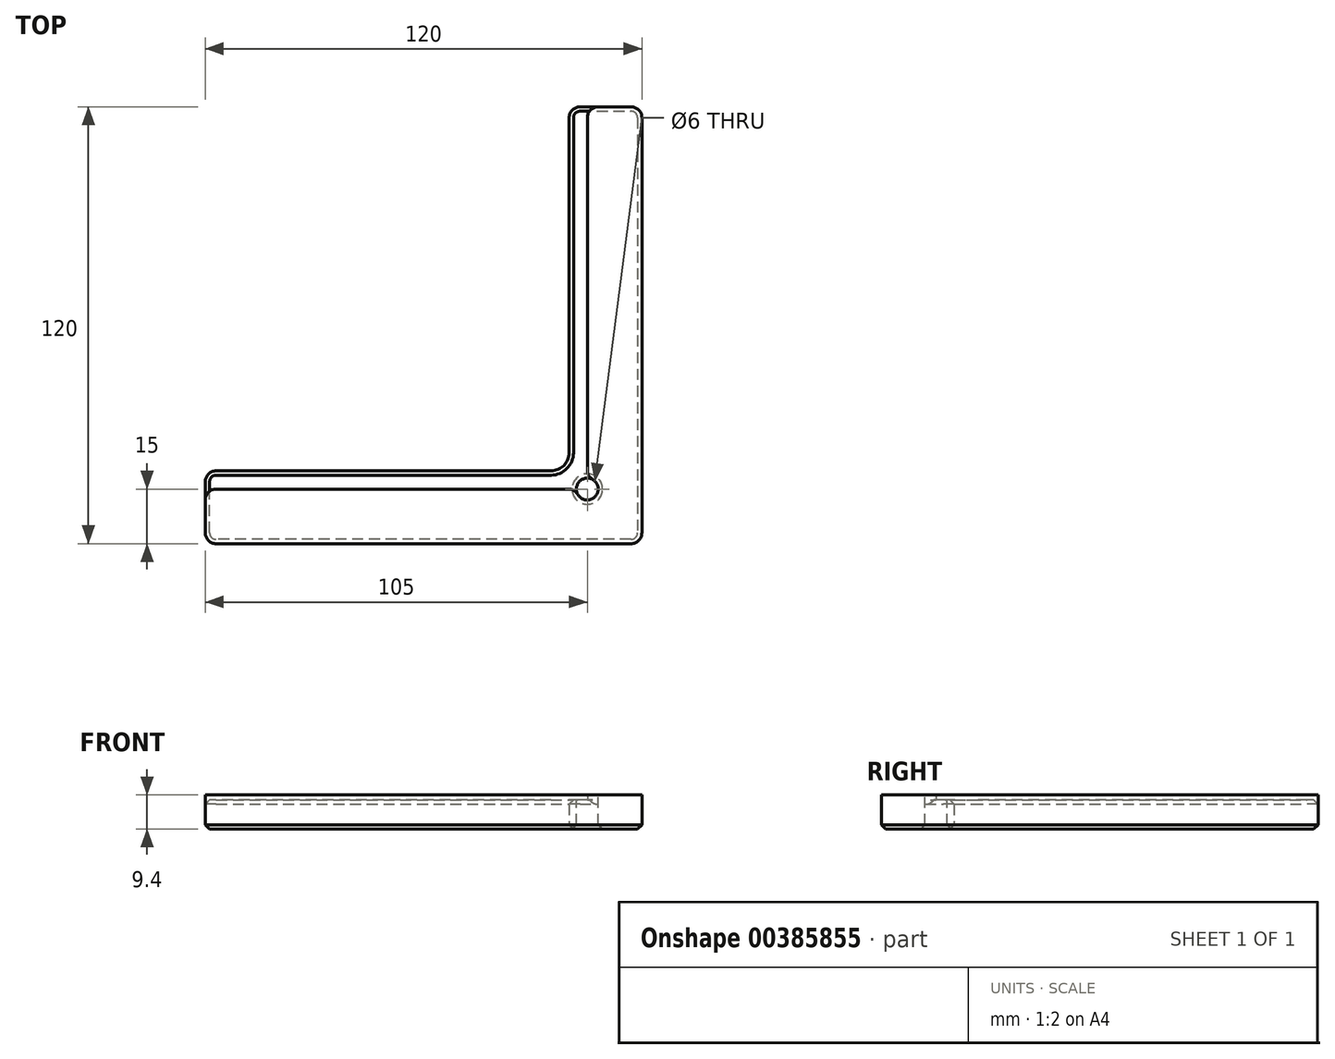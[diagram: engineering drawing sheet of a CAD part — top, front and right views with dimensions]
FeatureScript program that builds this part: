
annotation { "Feature Type Name" : "Feature", "Feature Type Description" : "" }
export const myFeature = defineFeature(function(context is Context, id is Id, definition is map)
    precondition{}
    {
        {
            var Q0;
            Q0=qCreatedBy(makeId("Top.planeOp"),FACE);
            var sketch = newSketch(context, id + "F0", { "sketchPlane" : qUnion([Q0])});
            skLineSegment(sketch, "E0", {"start": v(0, 120) * mm, "end": v(0, 0) * mm});
            skLineSegment(sketch, "E1", {"start": v(0, 0) * mm, "end": v(-120, 0) * mm});
            skLineSegment(sketch, "E2", {"start": v(-120, 0) * mm, "end": v(-120, 20) * mm});
            skLineSegment(sketch, "E3", {"start": v(-120, 20) * mm, "end": v(-20, 20) * mm});
            skLineSegment(sketch, "E4", {"start": v(-20, 20) * mm, "end": v(-20, 120) * mm});
            skLineSegment(sketch, "E5", {"start": v(-20, 120) * mm, "end": v(0, 120) * mm});
            skSolve(sketch);
        }
        {
            var Q0;
            Q0 = qSketchRegion(id + "F0", true);
            extrude(context, id + "F1", {"entities" : qUnion([Q0]), "depth" : 8 * mm});
        }
        {
            var Q0;
            Q0=makeQuery(id+"F1.opExtrude","CAP_FACE",FACE,{"disambiguationData":[OSD([sQuery(id+"F0.wireOp",EDGE,"E0"),sQuery(id+"F0.wireOp",EDGE,"E1"),sQuery(id+"F0.wireOp",EDGE,"E2"),sQuery(id+"F0.wireOp",EDGE,"E3"),sQuery(id+"F0.wireOp",EDGE,"E4"),sQuery(id+"F0.wireOp",EDGE,"E5")])],"isStart":false});
            var sketch = newSketch(context, id + "F2", { "sketchPlane" : qUnion([Q0])});
            skLineSegment(sketch, "E6.0", {"start": v(0, 0) * mm, "end": v(-120, 0) * mm});
            skLineSegment(sketch, "E6.1", {"start": v(0, 120) * mm, "end": v(0, 0) * mm});
            skLineSegment(sketch, "E7", {"start": v(-120, 0) * mm, "end": v(-120, 15) * mm});
            skLineSegment(sketch, "E8", {"start": v(-120, 15) * mm, "end": v(-15, 15) * mm});
            skLineSegment(sketch, "E9", {"start": v(-15, 15) * mm, "end": v(-15, 120) * mm});
            skLineSegment(sketch, "E10", {"start": v(-15, 120) * mm, "end": v(0, 120) * mm});
            skSolve(sketch);
        }
        {
            var Q0;
            Q0 = qSketchRegion(id + "F2", true);
            extrude(context, id + "F3", {"entities" : qUnion([Q0]), "operationType" : NewBodyOperationType.ADD, "depth" : 1.4 * mm});
        }
        {
            var Q0;
            Q0=makeQuery(id+"F3.opExtrude","CAP_FACE",FACE,{"disambiguationData":[OSD([sQuery(id+"F2.wireOp",EDGE,"E6.0"),sQuery(id+"F2.wireOp",EDGE,"E6.1"),sQuery(id+"F2.wireOp",EDGE,"E7"),sQuery(id+"F2.wireOp",EDGE,"E8"),sQuery(id+"F2.wireOp",EDGE,"E9"),sQuery(id+"F2.wireOp",EDGE,"E10")])],"isStart":false});
            var sketch = newSketch(context, id + "F4", { "sketchPlane" : qUnion([Q0])});
            skCircle(sketch, "E11", {"center": v(-15, 15) * mm, "radius": 3 * mm});
            skSolve(sketch);
        }
        {
            var Q0;
            Q0 = qSketchRegion(id + "F4", true);
            extrude(context, id + "F5", {"entities" : qUnion([Q0]), "operationType" : NewBodyOperationType.REMOVE, "endBound" : BoundingType.THROUGH_ALL, "oppositeDirection" : true, "depth" : 25 * mm});
        }
        {
            var Q0;
            Q0=makeQuery(id+"F1.opExtrude","SWEPT_EDGE",EDGE,{"disambiguationData":[OSD([sQuery(id+"F0.wireOp",EDGE,"E3"),sQuery(id+"F0.wireOp",EDGE,"E4")])]});
            fillet(context, id + "F6", {"entities" : qUnion([Q0]), "radius" : 5 * mm, "tangentPropagation" : true, "allowEdgeOverflow" : false});
        }
        {
            var Q0;
            Q0=makeQuery(id+"F3.boolean.opBoolean","MERGE",EDGE,{"derivedFrom":[makeQuery(id+"F1.opExtrude","SWEPT_EDGE",EDGE,{"disambiguationData":[OSD([sQuery(id+"F0.wireOp",EDGE,"E0"),sQuery(id+"F0.wireOp",EDGE,"E1")])]}),makeQuery(id+"F3.opExtrude","SWEPT_EDGE",EDGE,{"disambiguationData":[OSD([sQuery(id+"F2.wireOp",EDGE,"E6.0"),sQuery(id+"F2.wireOp",EDGE,"E6.1")])]})]});
            var Q1;
            Q1=makeQuery(id+"F3.boolean.opBoolean","MERGE",EDGE,{"derivedFrom":[makeQuery(id+"F1.opExtrude","SWEPT_EDGE",EDGE,{"disambiguationData":[OSD([sQuery(id+"F0.wireOp",EDGE,"E0"),sQuery(id+"F0.wireOp",EDGE,"E5")])]}),makeQuery(id+"F3.opExtrude","SWEPT_EDGE",EDGE,{"disambiguationData":[OSD([sQuery(id+"F2.wireOp",EDGE,"E6.1"),sQuery(id+"F2.wireOp",EDGE,"E10")])]})]});
            var Q2;
            Q2=makeQuery(id+"F1.opExtrude","SWEPT_EDGE",EDGE,{"disambiguationData":[OSD([sQuery(id+"F0.wireOp",EDGE,"E4"),sQuery(id+"F0.wireOp",EDGE,"E5")])]});
            var Q3;
            Q3=makeQuery(id+"F1.opExtrude","SWEPT_EDGE",EDGE,{"disambiguationData":[OSD([sQuery(id+"F0.wireOp",EDGE,"E2"),sQuery(id+"F0.wireOp",EDGE,"E3")])]});
            var Q4;
            Q4=makeQuery(id+"F3.boolean.opBoolean","MERGE",EDGE,{"derivedFrom":[makeQuery(id+"F1.opExtrude","SWEPT_EDGE",EDGE,{"disambiguationData":[OSD([sQuery(id+"F0.wireOp",EDGE,"E1"),sQuery(id+"F0.wireOp",EDGE,"E2")])]}),makeQuery(id+"F3.opExtrude","SWEPT_EDGE",EDGE,{"disambiguationData":[OSD([sQuery(id+"F2.wireOp",EDGE,"E6.0"),sQuery(id+"F2.wireOp",EDGE,"E7")])]})]});
            var Q5;
            Q5=makeQuery(id+"F3.opExtrude","SWEPT_EDGE",EDGE,{"disambiguationData":[OSD([sQuery(id+"F0.wireOp",EDGE,"E2"),sQuery(id+"F2.wireOp",EDGE,"E7"),sQuery(id+"F2.wireOp",EDGE,"E8")])]});
            var Q6;
            Q6=makeQuery(id+"F5.boolean.opBoolean","INTERSECT",EDGE,{"derivedFrom":[makeQuery(id+"F3.opExtrude","SWEPT_FACE",FACE,{"disambiguationData":[OSD([sQuery(id+"F2.wireOp",EDGE,"E9")])]}),makeQuery(id+"F5.opExtrude","SWEPT_FACE",FACE,{"disambiguationData":[OSD([sQuery(id+"F4.wireOp",EDGE,"E11")])]})]});
            var Q7;
            Q7=makeQuery(id+"F5.boolean.opBoolean","INTERSECT",EDGE,{"derivedFrom":[makeQuery(id+"F3.opExtrude","SWEPT_FACE",FACE,{"disambiguationData":[OSD([sQuery(id+"F2.wireOp",EDGE,"E8")])]}),makeQuery(id+"F5.opExtrude","SWEPT_FACE",FACE,{"disambiguationData":[OSD([sQuery(id+"F4.wireOp",EDGE,"E11")])]})]});
            var Q8;
            Q8=makeQuery(id+"F3.opExtrude","SWEPT_EDGE",EDGE,{"disambiguationData":[OSD([sQuery(id+"F0.wireOp",EDGE,"E5"),sQuery(id+"F2.wireOp",EDGE,"E9"),sQuery(id+"F2.wireOp",EDGE,"E10")])]});
            fillet(context, id + "F7", {"entities" : qUnion([Q0, Q1, Q2, Q3, Q4, Q5, Q6, Q7, Q8]), "radius" : 3 * mm, "tangentPropagation" : true, "allowEdgeOverflow" : false});
        }
        {
            var Q0;
            Q0=makeQuery(id+"F1.opExtrude","CAP_EDGE",EDGE,{"disambiguationData":[OSD([sQuery(id+"F0.wireOp",EDGE,"E4")])],"isStart":false});
            chamfer(context, id + "F8", {"entities" : qUnion([Q0]), "width" : 1.2 * mm, "tangentPropagation" : true});
        }
        {
            var Q0;
            Q0=makeQuery(id+"F1.opExtrude","CAP_EDGE",EDGE,{"disambiguationData":[OSD([sQuery(id+"F0.wireOp",EDGE,"E1")])],"isStart":true});
            var Q1;
            Q1=makeQuery(id+"F5.boolean.opBoolean","INTERSECT",EDGE,{"derivedFrom":[makeQuery(id+"F1.opExtrude","CAP_FACE",FACE,{"disambiguationData":[OSD([sQuery(id+"F0.wireOp",EDGE,"E0"),sQuery(id+"F0.wireOp",EDGE,"E1"),sQuery(id+"F0.wireOp",EDGE,"E2"),sQuery(id+"F0.wireOp",EDGE,"E3"),sQuery(id+"F0.wireOp",EDGE,"E4"),sQuery(id+"F0.wireOp",EDGE,"E5")])],"isStart":true}),makeQuery(id+"F5.opExtrude","SWEPT_FACE",FACE,{"disambiguationData":[OSD([sQuery(id+"F4.wireOp",EDGE,"E11")])]})]});
            chamfer(context, id + "F9", {"entities" : qUnion([Q0, Q1]), "width" : 1.2 * mm, "tangentPropagation" : true});
        }
    });
